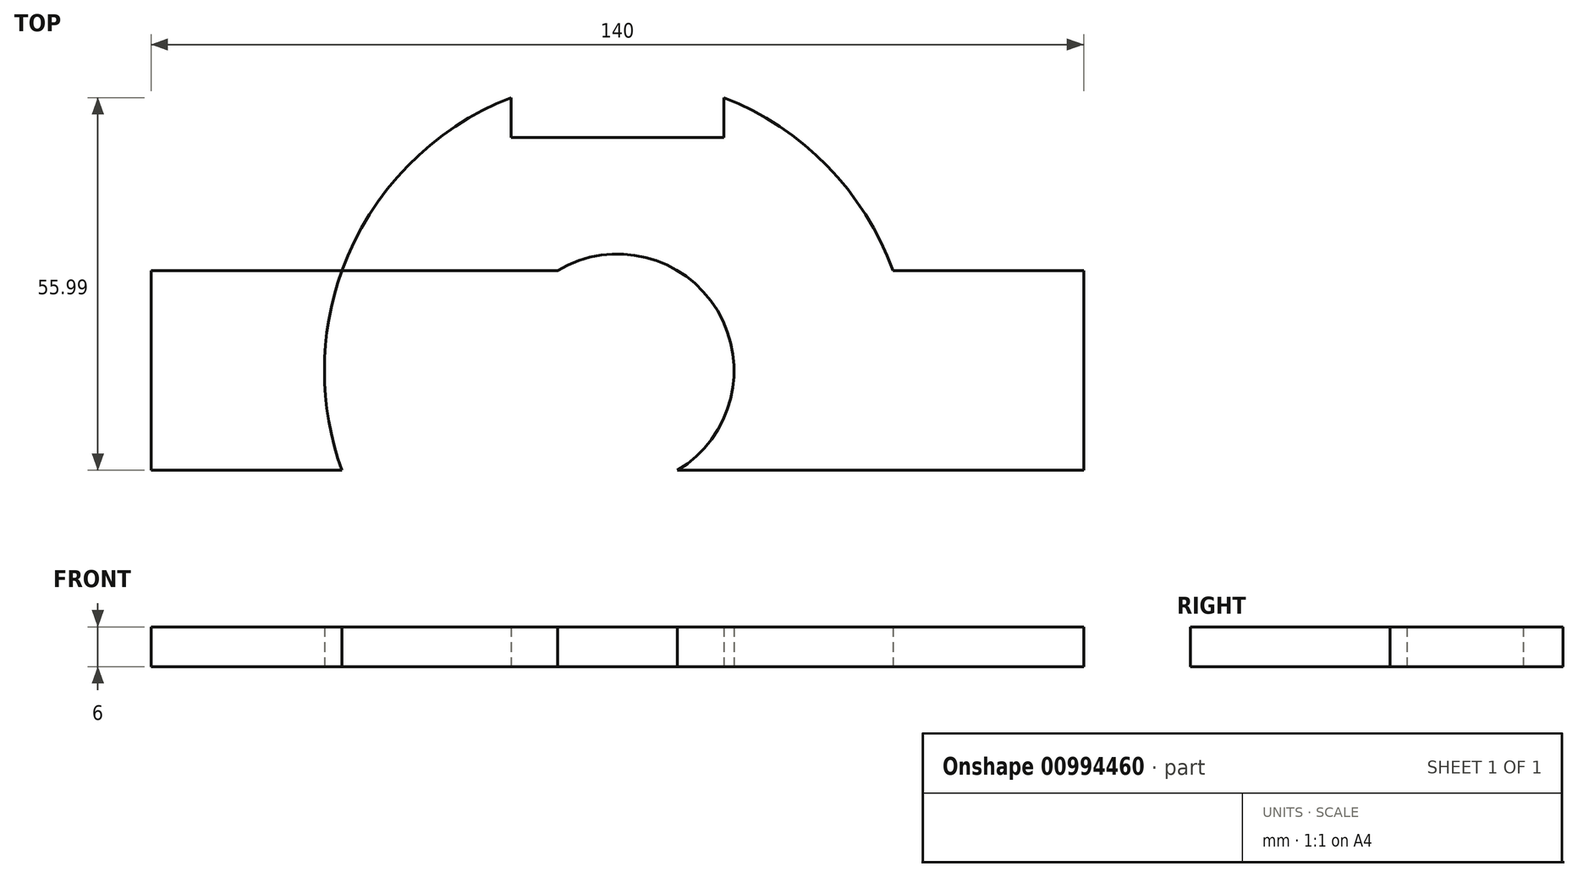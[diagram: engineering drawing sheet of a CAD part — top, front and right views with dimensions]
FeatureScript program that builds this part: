
annotation { "Feature Type Name" : "Feature", "Feature Type Description" : "" }
export const myFeature = defineFeature(function(context is Context, id is Id, definition is map)
    precondition{}
    {
        {
            var Q0;
            Q0=qCreatedBy(makeId("Top.planeOp"),FACE);
            var sketch = newSketch(context, id + "F0", { "sketchPlane" : qUnion([Q0])});
            skPoint(sketch, "E0", {"position": v(-22.79, 21.86) * mm});
            skPoint(sketch, "E1", {"position": v(31.21, 21.86) * mm});
            skPoint(sketch, "E2", {"position": v(4.21, 21.86) * mm});
            skPoint(sketch, "E3", {"position": v(4.21, -22.64) * mm});
            skPoint(sketch, "E4", {"position": v(-23.79, -22.64) * mm});
            skPoint(sketch, "E5", {"position": v(32.21, -22.64) * mm});
            skPoint(sketch, "E6", {"position": v(4.21, 2.61) * mm});
            skCircle(sketch, "E7", {"center": v(4.21, 2.61) * mm, "radius": 17.5 * mm});
            skCircle(sketch, "E8", {"center": v(4.21, 2.61) * mm, "radius": 44 * mm});
            skLineSegment(sketch, "E9.bottom", {"start": v(-11.79, 48) * mm, "end": v(20.21, 48) * mm});
            skLineSegment(sketch, "E9.top", {"start": v(-11.79, 37.63) * mm, "end": v(20.21, 37.63) * mm});
            skLineSegment(sketch, "E9.left", {"start": v(-11.79, 48) * mm, "end": v(-11.79, 37.63) * mm});
            skLineSegment(sketch, "E9.right", {"start": v(20.21, 48) * mm, "end": v(20.21, 37.63) * mm});
            skPoint(sketch, "E10", {"position": v(4.21, 37.63) * mm});
            skLineSegment(sketch, "E11.bottom", {"start": v(-65.79, 17.61) * mm, "end": v(74.21, 17.61) * mm});
            skLineSegment(sketch, "E11.top", {"start": v(-65.79, -12.39) * mm, "end": v(74.21, -12.39) * mm});
            skLineSegment(sketch, "E11.left", {"start": v(-65.79, 17.61) * mm, "end": v(-65.79, -12.39) * mm});
            skLineSegment(sketch, "E11.right", {"start": v(74.21, 17.61) * mm, "end": v(74.21, -12.39) * mm});
            skPoint(sketch, "E12", {"position": v(-33.79, 2.61) * mm});
            skPoint(sketch, "E13", {"position": v(-41.79, 2.61) * mm});
            skPoint(sketch, "E14", {"position": v(-49.79, 2.61) * mm});
            skPoint(sketch, "E15", {"position": v(-57.79, 2.61) * mm});
            skPoint(sketch, "E16", {"position": v(42.21, 2.61) * mm});
            skPoint(sketch, "E17", {"position": v(50.21, 2.61) * mm});
            skPoint(sketch, "E18", {"position": v(58.21, 2.61) * mm});
            skPoint(sketch, "E19", {"position": v(66.21, 2.61) * mm});
            skPoint(sketch, "E20", {"position": v(-25.79, 2.61) * mm});
            skPoint(sketch, "E21", {"position": v(-17.79, 2.61) * mm});
            skPoint(sketch, "E22", {"position": v(34.21, 2.61) * mm});
            skPoint(sketch, "E23", {"position": v(26.21, 2.61) * mm});
            skSolve(sketch);
        }
        {
            var Q0;
            {var subQ5=sQuery(id+"F0.wireOp",EDGE,"E11.left");Q0=makeQuery(id+"F0.imprint","IMPRINT",FACE,{"disambiguationData":[TD([[makeQuery(id+"F0.imprint","IMPRINT",EDGE,{"derivedFrom":subQ5}),1.0]])]});}
            var Q1;
            {var subQ0=sQuery(id+"F0.wireOp",EDGE,"E11.bottom");var subQ1=sQuery(id+"F0.wireOp",EDGE,"E7");var subQ2=makeQuery(id+"F0.imprint","INTERSECT",VERTEX,{"disambiguationData":[OD(0.0)],"derivedFrom":[subQ1,subQ0]});Q1=makeQuery(id+"F0.imprint","IMPRINT",FACE,{"disambiguationData":[TD([[makeQuery(id+"F0.imprint","IMPRINT",EDGE,{"disambiguationData":[TD([[subQ2,-1.0]])],"derivedFrom":subQ1}),-1.0]])]});}
            var Q2;
            {var subQ0=sQuery(id+"F0.wireOp",EDGE,"E11.bottom");var subQ1=sQuery(id+"F0.wireOp",EDGE,"E7");var subQ2=makeQuery(id+"F0.imprint","INTERSECT",VERTEX,{"disambiguationData":[OD(1.0)],"derivedFrom":[subQ1,subQ0]});Q2=makeQuery(id+"F0.imprint","IMPRINT",FACE,{"disambiguationData":[TD([[makeQuery(id+"F0.imprint","IMPRINT",EDGE,{"disambiguationData":[TD([[subQ2,1.0]])],"derivedFrom":subQ1}),-1.0]])]});}
            var Q3;
            {var subQ5=sQuery(id+"F0.wireOp",EDGE,"E11.right");Q3=makeQuery(id+"F0.imprint","IMPRINT",FACE,{"disambiguationData":[TD([[makeQuery(id+"F0.imprint","IMPRINT",EDGE,{"derivedFrom":subQ5}),-1.0]])]});}
            var Q4;
            {var subQ0=sQuery(id+"F0.wireOp",EDGE,"E9.top");Q4=makeQuery(id+"F0.imprint","IMPRINT",FACE,{"disambiguationData":[TD([[makeQuery(id+"F0.imprint","IMPRINT",EDGE,{"derivedFrom":subQ0}),-1.0]])]});}
            var Q5;
            {var subQ0=sQuery(id+"F0.wireOp",EDGE,"E11.top");var subQ1=sQuery(id+"F0.wireOp",EDGE,"E7");var subQ2=makeQuery(id+"F0.imprint","INTERSECT",VERTEX,{"disambiguationData":[OD(0.0)],"derivedFrom":[subQ1,subQ0]});Q5=makeQuery(id+"F0.imprint","IMPRINT",FACE,{"disambiguationData":[TD([[makeQuery(id+"F0.imprint","IMPRINT",EDGE,{"disambiguationData":[TD([[subQ2,-1.0]])],"derivedFrom":subQ1}),-1.0]])]});}
            extrude(context, id + "F1", {"entities" : qUnion([Q0, Q1, Q2, Q3, Q4, Q5]), "depth" : 6 * mm, "offsetDistance" : 25 * mm});
        }
    });
